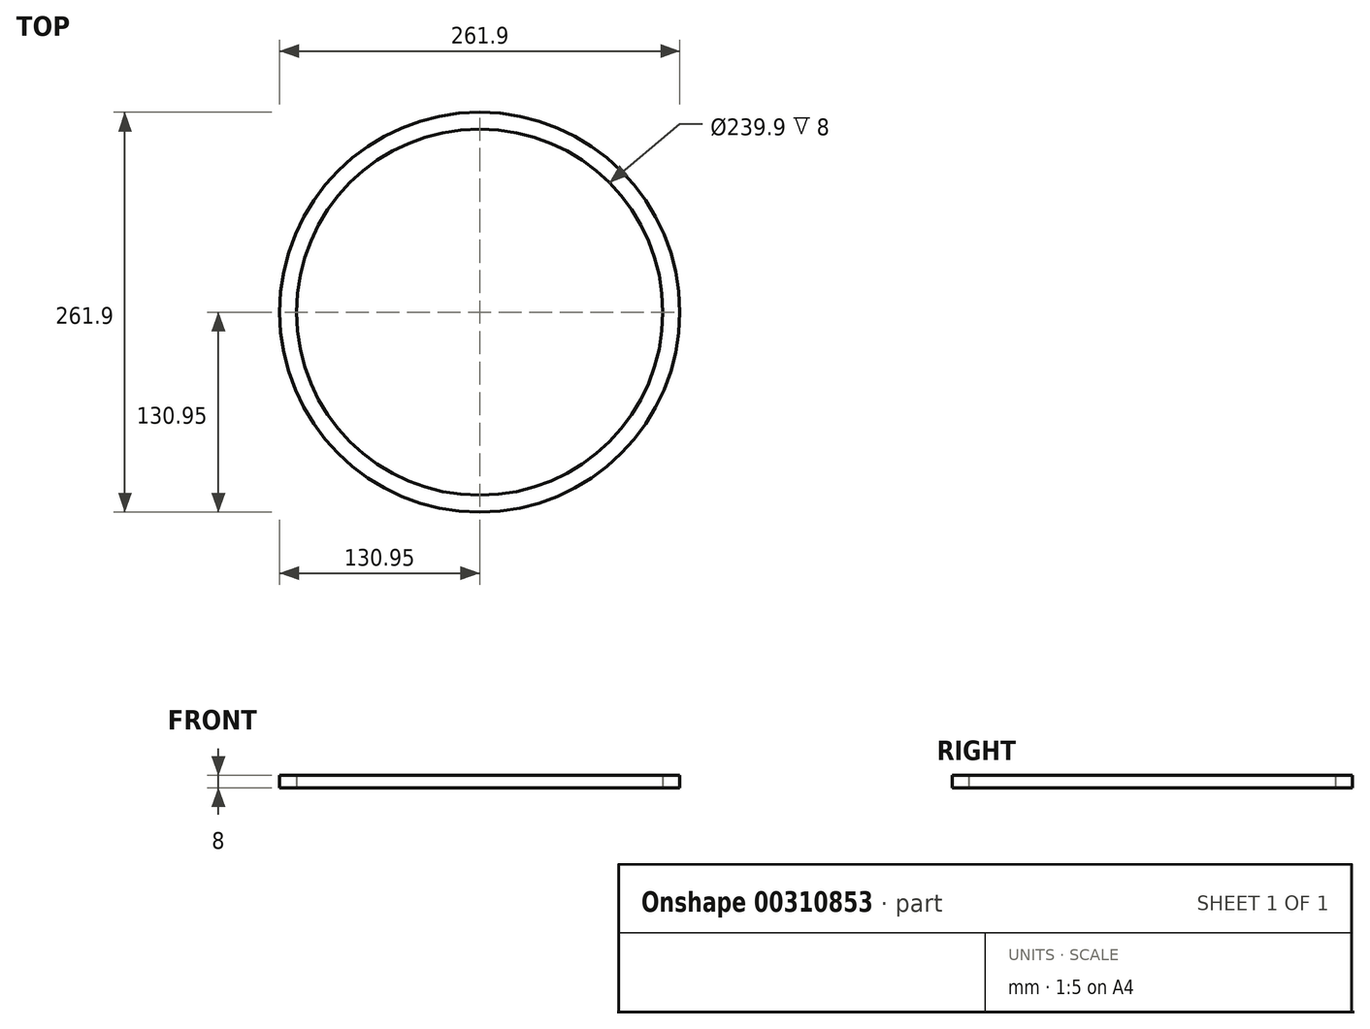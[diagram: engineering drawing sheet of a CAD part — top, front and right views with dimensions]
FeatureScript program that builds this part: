
annotation { "Feature Type Name" : "Feature", "Feature Type Description" : "" }
export const myFeature = defineFeature(function(context is Context, id is Id, definition is map)
    precondition{}
    {
        {
            var Q0;
            Q0=qCreatedBy(makeId("Top.planeOp"),FACE);
            var sketch = newSketch(context, id + "F0", { "sketchPlane" : qUnion([Q0])});
            skCircle(sketch, "E0", {"center": v(0, 0) * mm, "radius": 130.95 * mm});
            skCircle(sketch, "E1", {"center": v(0, 0) * mm, "radius": 119.95 * mm});
            skSolve(sketch);
        }
        {
            var Q0;
            Q0=makeQuery(id+"F0.imprint","IMPRINT",FACE,{"disambiguationData":[TD([[makeQuery(id+"F0.imprint","IMPRINT",EDGE,{"derivedFrom":sQuery(id+"F0.wireOp",EDGE,"E0")}),1.0]])]});
            extrude(context, id + "F1", {"entities" : qUnion([Q0]), "depth" : 8 * mm});
        }
    });
